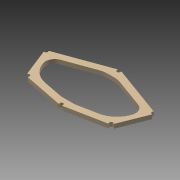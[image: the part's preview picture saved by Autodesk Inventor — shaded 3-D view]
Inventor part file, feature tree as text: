
AUTODESK INVENTOR PART (.ipt)
format: ipt  version: 2015 (Build 190159000, 159)  size: 176,640 bytes
history: native  units: mm
features: fillet x10, hole x4, extrude x2, sketch x2, mirror x1
ambient origin geometry x8: Origin, YZ Plane, XZ Plane, XY Plane, X Axis, Y Axis, Z Axis, Center Point
bodies: Solid4 (feature_tree)
feature tree (19):
  extrude  "Extrusion4"  Depth=272.1864mm
  hole  "Hole2"  [1 undecoded]
  hole  "Hole3"  [1 undecoded]
  hole  "Hole4"  [1 undecoded]
  hole  "Hole5"  [1 undecoded]
  extrude  "Extrusion6"  Depth=2.0mm
  fillet  "Fillet6"  Radius=18.0mm
  fillet  "Fillet7"  Radius=23.0mm
  fillet  "Fillet8"  Radius=28.0mm
  fillet  "Fillet9"  Radius=28.0mm
  fillet  "Fillet10"  Radius=30.0mm
  fillet  "Fillet11"  [1 undecoded]
  fillet  "Fillet12"  Radius=30.0mm
  fillet  "Fillet13"  Radius=10.0mm
  fillet  "Fillet14"  Radius=40.0mm
  fillet  "Fillet15"  Radius=100.0mm
  mirror  "Mirror3"
  sketch  "Sketch1"  dims[d9=272.1864mm d11=240.1824mm]
  sketch  "Sketch6"  dims[d15=184.7088mm d20=185.3184mm d22=46.3296mm d39=0.0mm d41=0.0mm d42=9.7536mm d98=18.0mm d99=0.0mm d140=10.0mm d141=10.0mm d102=15.0mm d103=6.0mm d104=3.023mm d105=2.0mm d106=14.3117mm d107=8.0mm d108=20.594885mm d144=10.0mm d145=10.0mm d111=15.0mm d112=6.0mm d113=3.023mm d114=2.0mm d115=14.3117mm d116=8.0mm d117=20.594885mm d142=10.0mm d143=10.0mm d124=15.0mm d125=6.0mm d126=3.023mm d127=2.0mm d128=14.3117mm d129=8.0mm d130=20.594885mm d146=10.0mm d147=10.0mm d133=15.0mm d134=6.0mm d135=3.023mm d136=2.0mm d137=14.3117mm d138=8.0mm d139=20.594885mm d167=23.0mm d168=28.0mm d170=28.0mm d171=30.0mm d173=0.0mm d174=30.0mm d175=10.0mm d176=0.0mm d185=40.0mm d186=100.0mm d187=100.0mm d188=100.0mm d189=1.5mm d190=1.0mm d191=1.0mm d192=2.0mm d193=2.0mm d194=2.0mm]
note: 5 required parameter values undecoded (feature->parameter linkage not recoverable at this tier; creation-order binding heuristic only, values carry confidence <= 0.55)
